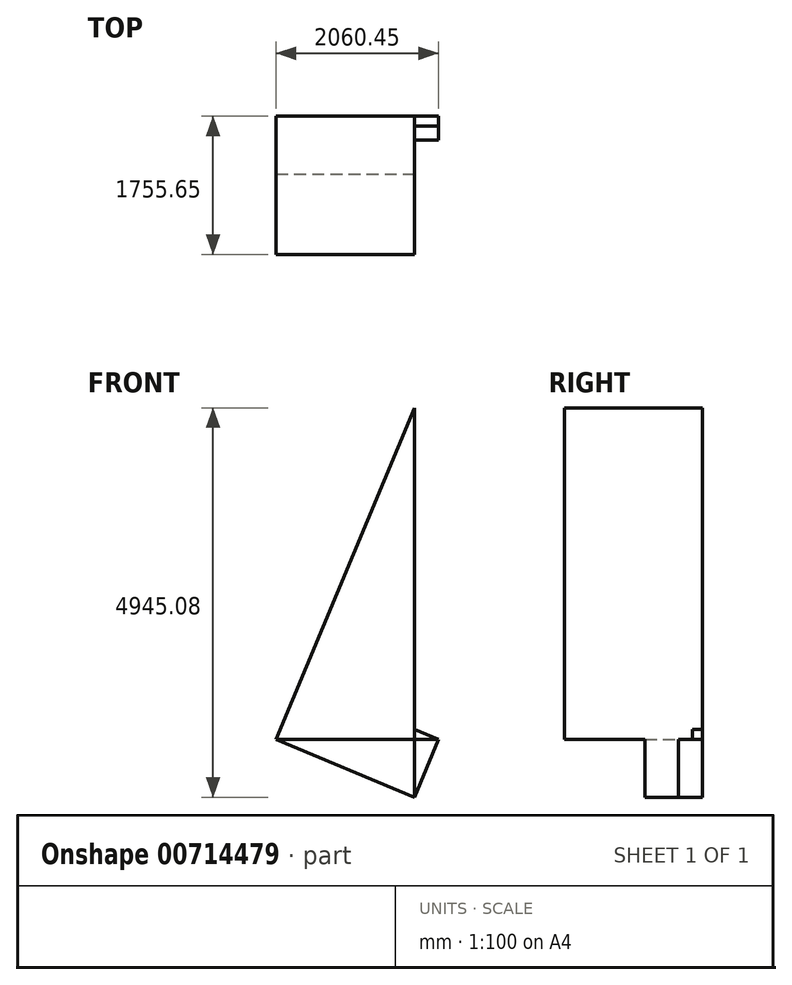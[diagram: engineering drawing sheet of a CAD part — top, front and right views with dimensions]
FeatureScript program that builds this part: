
annotation { "Feature Type Name" : "Feature", "Feature Type Description" : "" }
export const myFeature = defineFeature(function(context is Context, id is Id, definition is map)
    precondition{}
    {
        {
            var Q0;
            Q0=qCreatedBy(makeId("Front.planeOp"),FACE);
            var sketch = newSketch(context, id + "F0", { "sketchPlane" : qUnion([Q0])});
            skLineSegment(sketch, "E0", {"start": v(0, 0) * mm, "end": v(304.8, 0) * mm});
            skLineSegment(sketch, "E1", {"start": v(304.8, 0) * mm, "end": v(0, 127) * mm});
            skLineSegment(sketch, "E2", {"start": v(0, 127) * mm, "end": v(0, 0) * mm});
            skSolve(sketch);
        }
        {
            var Q0;
            Q0=makeQuery(id+"F0.imprint","IMPRINT",FACE,{"disambiguationData":[TD([[makeQuery(id+"F0.imprint","IMPRINT",EDGE,{"derivedFrom":sQuery(id+"F0.wireOp",EDGE,"E0")}),1.0]])]});
            extrude(context, id + "F1", {"entities" : qUnion([Q0]), "depth" : 127 * mm, "offsetDistance" : 25.4 * mm});
        }
        {
            var Q0;
            Q0=qCreatedBy(makeId("Front.planeOp"),FACE);
            var sketch = newSketch(context, id + "F2", { "sketchPlane" : qUnion([Q0])});
            skLineSegment(sketch, "E3", {"start": v(0, 0) * mm, "end": v(304.8, 0) * mm});
            skLineSegment(sketch, "E4", {"start": v(304.8, 0) * mm, "end": v(0, -731.52) * mm});
            skLineSegment(sketch, "E5", {"start": v(0, -731.52) * mm, "end": v(0, 0) * mm});
            skSolve(sketch);
        }
        {
            var Q0;
            Q0 = qSketchRegion(id + "F2", true);
            extrude(context, id + "F3", {"entities" : qUnion([Q0]), "operationType" : NewBodyOperationType.ADD, "depth" : 304.8 * mm, "offsetDistance" : 25.4 * mm});
        }
        {
            var Q0;
            Q0=qCreatedBy(makeId("Front.planeOp"),FACE);
            var sketch = newSketch(context, id + "F4", { "sketchPlane" : qUnion([Q0])});
            skLineSegment(sketch, "E6", {"start": v(0, -731.52) * mm, "end": v(0, 0) * mm});
            skLineSegment(sketch, "E7", {"start": v(0, 0) * mm, "end": v(-1755.65, 0) * mm});
            skLineSegment(sketch, "E8", {"start": v(-1755.65, 0) * mm, "end": v(0, -731.52) * mm});
            skSolve(sketch);
        }
        {
            var Q0;
            Q0 = qSketchRegion(id + "F4", true);
            extrude(context, id + "F5", {"entities" : qUnion([Q0]), "operationType" : NewBodyOperationType.ADD, "depth" : 731.52 * mm, "offsetDistance" : 25.4 * mm});
        }
        {
            var Q0;
            Q0=qCreatedBy(makeId("Front.planeOp"),FACE);
            var sketch = newSketch(context, id + "F6", { "sketchPlane" : qUnion([Q0])});
            skLineSegment(sketch, "E9.0", {"start": v(0, 0) * mm, "end": v(-1755.65, 0) * mm});
            skLineSegment(sketch, "E10", {"start": v(0, 0) * mm, "end": v(0, 4213.56) * mm});
            skLineSegment(sketch, "E11", {"start": v(0, 4213.56) * mm, "end": v(-1755.65, 0) * mm});
            skSolve(sketch);
        }
        {
            var Q0;
            Q0 = qSketchRegion(id + "F6", true);
            extrude(context, id + "F7", {"entities" : qUnion([Q0]), "operationType" : NewBodyOperationType.ADD, "depth" : 1755.65 * mm, "offsetDistance" : 25.4 * mm});
        }
    });
